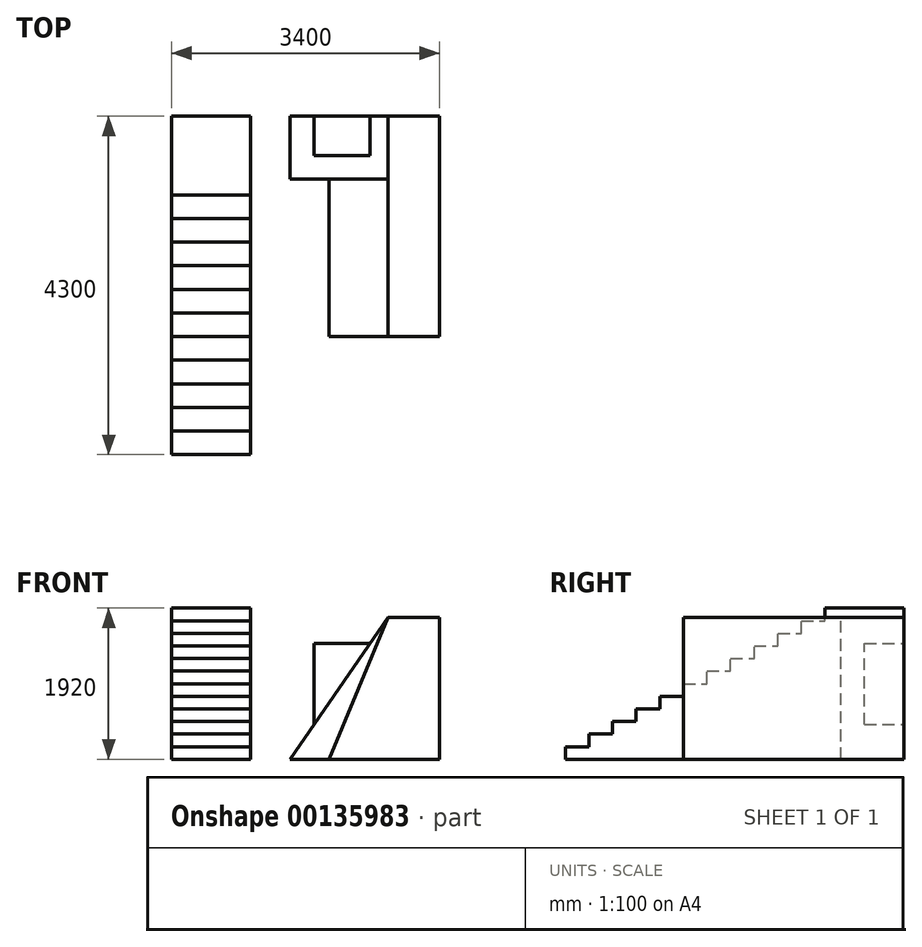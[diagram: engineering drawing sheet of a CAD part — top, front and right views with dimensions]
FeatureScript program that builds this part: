
annotation { "Feature Type Name" : "Feature", "Feature Type Description" : "" }
export const myFeature = defineFeature(function(context is Context, id is Id, definition is map)
    precondition{}
    {
        {
            var Q0;
            Q0=qCreatedBy(makeId("Front.planeOp"),FACE);
            var sketch = newSketch(context, id + "F0", { "sketchPlane" : qUnion([Q0])});
            skLineSegment(sketch, "E0", {"start": v(0, 0) * mm, "end": v(-1400, 0) * mm});
            skLineSegment(sketch, "E1", {"start": v(-1400, 0) * mm, "end": v(-650, 1800) * mm});
            skLineSegment(sketch, "E2", {"start": v(-650, 1800) * mm, "end": v(0, 1800) * mm});
            skLineSegment(sketch, "E3", {"start": v(0, 1800) * mm, "end": v(0, 0) * mm});
            skSolve(sketch);
        }
        {
            var Q0;
            Q0=makeQuery(id+"F0.imprint","IMPRINT",FACE,{"disambiguationData":[TD([[makeQuery(id+"F0.imprint","IMPRINT",EDGE,{"derivedFrom":sQuery(id+"F0.wireOp",EDGE,"E0")}),-1.0]])]});
            extrude(context, id + "F1", {"entities" : qUnion([Q0]), "depth" : 2000 * mm});
        }
        {
            var Q0;
            Q0=makeQuery(id+"F1.opExtrude","CAP_FACE",FACE,{"disambiguationData":[OSD([sQuery(id+"F0.wireOp",EDGE,"E0"),sQuery(id+"F0.wireOp",EDGE,"E1"),sQuery(id+"F0.wireOp",EDGE,"E2"),sQuery(id+"F0.wireOp",EDGE,"E3")])],"isStart":true});
            var sketch = newSketch(context, id + "F2", { "sketchPlane" : qUnion([Q0])});
            skLineSegment(sketch, "E4", {"start": v(0, 0) * mm, "end": v(1900, 0) * mm});
            skLineSegment(sketch, "E5", {"start": v(1900, 0) * mm, "end": v(650, 1800) * mm});
            skLineSegment(sketch, "E6", {"start": v(650, 1800) * mm, "end": v(0, 1800) * mm});
            skLineSegment(sketch, "E7", {"start": v(0, 1800) * mm, "end": v(0, 0) * mm});
            skSolve(sketch);
        }
        {
            var Q0;
            {var subQ2=sQuery(id+"F2.wireOp",EDGE,"E5");Q0=makeQuery(id+"F2.imprint","IMPRINT",FACE,{"disambiguationData":[TD([[makeQuery(id+"F2.imprint","IMPRINT",EDGE,{"derivedFrom":subQ2}),1.0]])]});}
            var Q1;
            Q1=makeQuery(id+"F2.imprint","IMPRINT",FACE,{"disambiguationData":[TD([[makeQuery(id+"F2.imprint","IMPRINT",EDGE,{"derivedFrom":sQuery(id+"F2.wireOp",EDGE,"E6")}),1.0]])]});
            extrude(context, id + "F3", {"entities" : qUnion([Q0, Q1]), "depth" : 800 * mm});
        }
        {
            var Q0;
            Q0=makeQuery(id+"F1.opExtrude","SWEPT_BODY",BODY,{"disambiguationData":[OSD([sQuery(id+"F0.wireOp",EDGE,"E0"),sQuery(id+"F0.wireOp",EDGE,"E1"),sQuery(id+"F0.wireOp",EDGE,"E2"),sQuery(id+"F0.wireOp",EDGE,"E3")])]});
            var Q1;
            Q1=makeQuery(id+"F3.opExtrude","SWEPT_BODY",BODY,{"disambiguationData":[OSD([sQuery(id+"F2.wireOp",EDGE,"E4"),sQuery(id+"F2.wireOp",EDGE,"E5"),sQuery(id+"F2.wireOp",EDGE,"E6"),sQuery(id+"F2.wireOp",EDGE,"E7")])]});
            booleanBodies(context, id + "F4", {"operationType" : BooleanOperationType.UNION, "tools" : qUnion([Q0, Q1])});
        }
        {
            var Q0;
            Q0=makeQuery(id+"F4.opBoolean","MERGE",FACE,{"derivedFrom":[makeQuery(id+"F1.opExtrude","SWEPT_FACE",FACE,{"disambiguationData":[OSD([sQuery(id+"F0.wireOp",EDGE,"E3")])]}),makeQuery(id+"F3.opExtrude","SWEPT_FACE",FACE,{"disambiguationData":[OSD([sQuery(id+"F2.wireOp",EDGE,"E7")])]})]});
            cPlane(context, id + "F5", {"entities" : qUnion([Q0]), "cplaneType" : CPlaneType.OFFSET, "offset" : 2400 * mm, "oppositeDirection" : true, "width" : 150 * mm, "height" : 150 * mm});
        }
        {
            var Q0;
            Q0=qCreatedBy(id+"F5.planeOp",FACE);
            var sketch = newSketch(context, id + "F6", { "sketchPlane" : qUnion([Q0])});
            skLineSegment(sketch, "E8", {"start": v(-3500, 0) * mm, "end": v(-3500, 160) * mm});
            skLineSegment(sketch, "E9", {"start": v(-3500, 160) * mm, "end": v(-3200, 160) * mm});
            skLineSegment(sketch, "E10", {"start": v(-3200, 160) * mm, "end": v(-3200, 320) * mm});
            skLineSegment(sketch, "E11", {"start": v(-3200, 320) * mm, "end": v(-2900, 320) * mm});
            skLineSegment(sketch, "E12", {"start": v(-2900, 320) * mm, "end": v(-2900, 480) * mm});
            skLineSegment(sketch, "E13", {"start": v(-2900, 480) * mm, "end": v(-2600, 480) * mm});
            skLineSegment(sketch, "E14", {"start": v(-2600, 480) * mm, "end": v(-2600, 640) * mm});
            skLineSegment(sketch, "E15", {"start": v(-2600, 640) * mm, "end": v(-2300, 640) * mm});
            skLineSegment(sketch, "E16", {"start": v(-2300, 640) * mm, "end": v(-2300, 800) * mm});
            skLineSegment(sketch, "E17", {"start": v(-2300, 800) * mm, "end": v(-2000, 800) * mm});
            skLineSegment(sketch, "E18", {"start": v(-2000, 800) * mm, "end": v(-2000, 960) * mm});
            skLineSegment(sketch, "E19", {"start": v(-2000, 960) * mm, "end": v(-1700, 960) * mm});
            skLineSegment(sketch, "E20", {"start": v(-1700, 960) * mm, "end": v(-1700, 1120) * mm});
            skLineSegment(sketch, "E21", {"start": v(-1700, 1120) * mm, "end": v(-1400, 1120) * mm});
            skLineSegment(sketch, "E22", {"start": v(800, 0) * mm, "end": v(-3500, 0) * mm});
            skLineSegment(sketch, "E23", {"start": v(-1400, 1120) * mm, "end": v(-1400, 1280) * mm});
            skLineSegment(sketch, "E24", {"start": v(-1400, 1280) * mm, "end": v(-1100, 1280) * mm});
            skLineSegment(sketch, "E25", {"start": v(-1100, 1280) * mm, "end": v(-1100, 1440) * mm});
            skLineSegment(sketch, "E26", {"start": v(-1100, 1440) * mm, "end": v(-800, 1440) * mm});
            skLineSegment(sketch, "E27", {"start": v(-800, 1440) * mm, "end": v(-800, 1600) * mm});
            skLineSegment(sketch, "E28", {"start": v(-800, 1600) * mm, "end": v(-500, 1600) * mm});
            skLineSegment(sketch, "E29", {"start": v(-500, 1600) * mm, "end": v(-500, 1760) * mm});
            skLineSegment(sketch, "E30", {"start": v(-500, 1760) * mm, "end": v(-200, 1760) * mm});
            skLineSegment(sketch, "E31", {"start": v(-200, 1760) * mm, "end": v(-200, 1920) * mm});
            skLineSegment(sketch, "E32", {"start": v(-200, 1920) * mm, "end": v(800, 1920) * mm});
            skLineSegment(sketch, "E33", {"start": v(800, 0) * mm, "end": v(800, 1920) * mm});
            skSolve(sketch);
        }
        {
            var Q0;
            Q0=makeQuery(id+"F6.imprint","IMPRINT",FACE,{"disambiguationData":[TD([[makeQuery(id+"F6.imprint","IMPRINT",EDGE,{"derivedFrom":sQuery(id+"F6.wireOp",EDGE,"E8")}),-1.0]])]});
            extrude(context, id + "F7", {"entities" : qUnion([Q0]), "oppositeDirection" : true, "depth" : 1000 * mm});
        }
        {
            var Q0;
            Q0=makeQuery(id+"F3.opExtrude","CAP_FACE",FACE,{"disambiguationData":[OSD([sQuery(id+"F2.wireOp",EDGE,"E4"),sQuery(id+"F2.wireOp",EDGE,"E5"),sQuery(id+"F2.wireOp",EDGE,"E6"),sQuery(id+"F2.wireOp",EDGE,"E7")])],"isStart":false});
            var sketch = newSketch(context, id + "F8", { "sketchPlane" : qUnion([Q0])});
            skLineSegment(sketch, "E34.bottom", {"start": v(688.11, 1469.68) * mm, "end": v(1592.54, 1469.68) * mm});
            skLineSegment(sketch, "E34.top", {"start": v(688.11, 295.1) * mm, "end": v(1592.54, 295.1) * mm});
            skLineSegment(sketch, "E34.left", {"start": v(688.11, 1469.68) * mm, "end": v(688.11, 295.1) * mm});
            skLineSegment(sketch, "E34.right", {"start": v(1592.54, 1469.68) * mm, "end": v(1592.54, 295.1) * mm});
            skSolve(sketch);
        }
        {
            var Q0;
            {var subQ0=sQuery(id+"F8.wireOp",EDGE,"E34.right");var subQ1=sQuery(id+"F8.wireOp",EDGE,"E34.bottom");var subQ2=makeQuery(id+"F8.imprint","INTERSECT",VERTEX,{"derivedFrom":[subQ1,subQ0]});Q0=makeQuery(id+"F8.imprint","IMPRINT",FACE,{"disambiguationData":[TD([[makeQuery(id+"F8.imprint","IMPRINT",EDGE,{"disambiguationData":[TD([[subQ2,1.0]])],"derivedFrom":subQ1}),-1.0]])]});}
            extrude(context, id + "F9", {"entities" : qUnion([Q0]), "operationType" : NewBodyOperationType.ADD, "oppositeDirection" : true, "depth" : 500 * mm});
        }
    });
